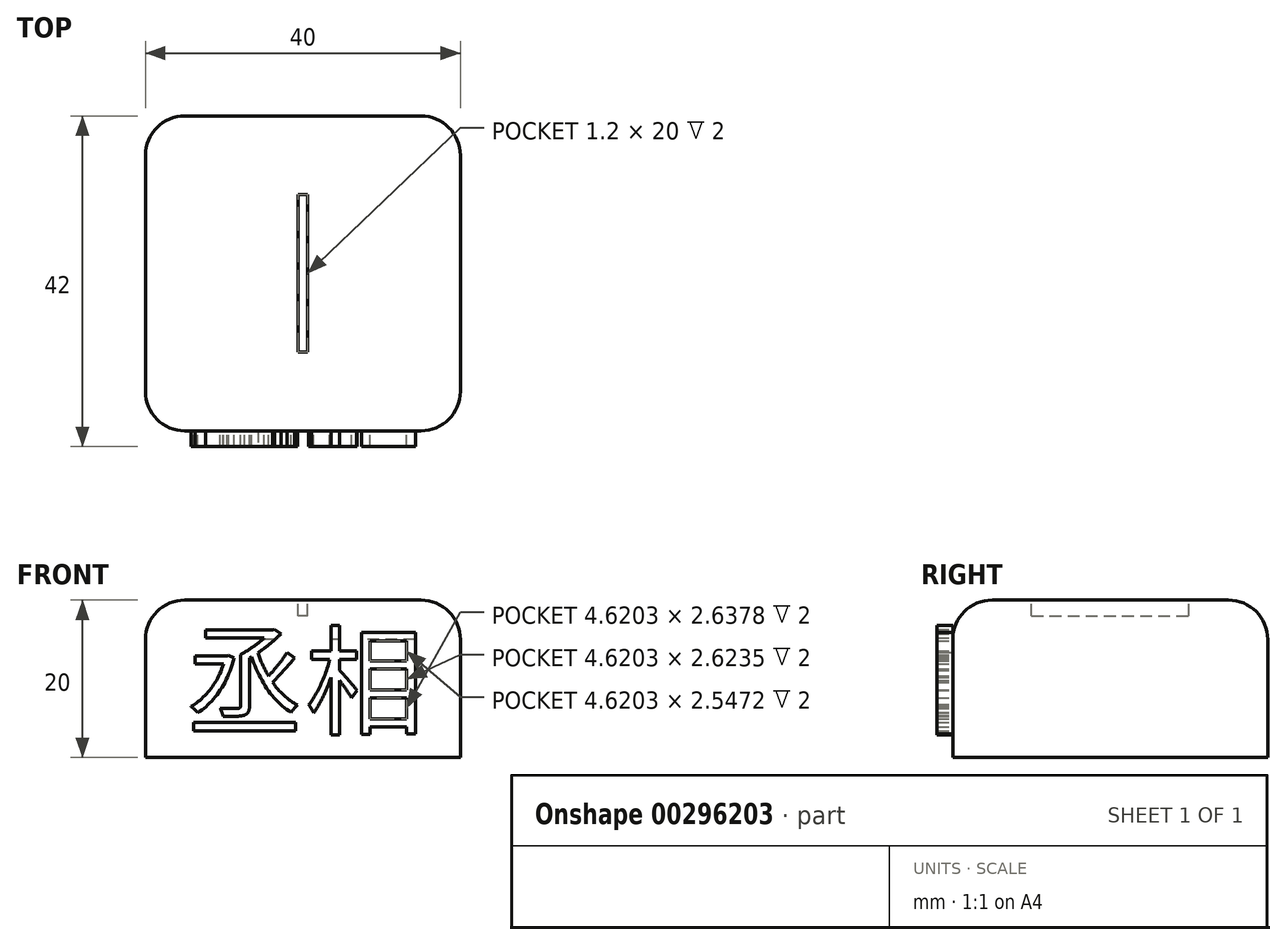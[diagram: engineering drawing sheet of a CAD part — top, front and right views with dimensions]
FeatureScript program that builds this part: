
annotation { "Feature Type Name" : "Feature", "Feature Type Description" : "" }
export const myFeature = defineFeature(function(context is Context, id is Id, definition is map)
    precondition{}
    {
        {
            var Q0;
            Q0=qCreatedBy(makeId("Top.planeOp"),FACE);
            var sketch = newSketch(context, id + "F0", { "sketchPlane" : qUnion([Q0])});
            skLineSegment(sketch, "E0.bottom", {"start": v(20, -20) * mm, "end": v(-20, -20) * mm});
            skLineSegment(sketch, "E0.top", {"start": v(20, 20) * mm, "end": v(-20, 20) * mm});
            skLineSegment(sketch, "E0.left", {"start": v(20, -20) * mm, "end": v(20, 20) * mm});
            skLineSegment(sketch, "E0.right", {"start": v(-20, -20) * mm, "end": v(-20, 20) * mm});
            skPoint(sketch, "E0.middle", {"position": v(0, 0) * mm});
            skLineSegment(sketch, "E1.bottom", {"start": v(0.6, -10) * mm, "end": v(-0.6, -10) * mm});
            skLineSegment(sketch, "E1.top", {"start": v(0.6, 10) * mm, "end": v(-0.6, 10) * mm});
            skLineSegment(sketch, "E1.left", {"start": v(0.6, -10) * mm, "end": v(0.6, 10) * mm});
            skLineSegment(sketch, "E1.right", {"start": v(-0.6, -10) * mm, "end": v(-0.6, 10) * mm});
            skSolve(sketch);
        }
        {
            var Q0;
            Q0=makeQuery(id+"F0.imprint","IMPRINT",FACE,{"disambiguationData":[TD([[makeQuery(id+"F0.imprint","IMPRINT",EDGE,{"derivedFrom":sQuery(id+"F0.wireOp",EDGE,"E0.bottom")}),-1.0]])]});
            var Q1;
            Q1=makeQuery(id+"F0.imprint","IMPRINT",FACE,{"disambiguationData":[TD([[makeQuery(id+"F0.imprint","IMPRINT",EDGE,{"derivedFrom":sQuery(id+"F0.wireOp",EDGE,"E1.bottom")}),-1.0]])]});
            extrude(context, id + "F1", {"entities" : qUnion([Q0, Q1]), "oppositeDirection" : true, "depth" : 20 * mm});
        }
        {
            var Q0;
            Q0=makeQuery(id+"F0.imprint","IMPRINT",FACE,{"disambiguationData":[TD([[makeQuery(id+"F0.imprint","IMPRINT",EDGE,{"derivedFrom":sQuery(id+"F0.wireOp",EDGE,"E1.bottom")}),-1.0]])]});
            extrude(context, id + "F2", {"entities" : qUnion([Q0]), "operationType" : NewBodyOperationType.REMOVE, "oppositeDirection" : true, "depth" : 2 * mm});
        }
        {
            var Q0;
            Q0=makeQuery(id+"F2.boolean.opBoolean","COPY",EDGE,{"derivedFrom":makeQuery(id+"F2.opExtrude","CAP_EDGE",EDGE,{"disambiguationData":[OSD([sQuery(id+"F0.wireOp",EDGE,"E1.left")])],"isStart":true})});
            var Q1;
            Q1=makeQuery(id+"F2.boolean.opBoolean","COPY",EDGE,{"derivedFrom":makeQuery(id+"F2.opExtrude","CAP_EDGE",EDGE,{"disambiguationData":[OSD([sQuery(id+"F0.wireOp",EDGE,"E1.right")])],"isStart":true})});
            var Q2;
            Q2=makeQuery(id+"F1.opExtrude","SWEPT_EDGE",EDGE,{"disambiguationData":[OSD([sQuery(id+"F0.wireOp",EDGE,"E0.bottom"),sQuery(id+"F0.wireOp",EDGE,"E0.left")])]});
            var Q3;
            Q3=makeQuery(id+"F1.opExtrude","SWEPT_EDGE",EDGE,{"disambiguationData":[OSD([sQuery(id+"F0.wireOp",EDGE,"E0.top"),sQuery(id+"F0.wireOp",EDGE,"E0.left")])]});
            var Q4;
            Q4=makeQuery(id+"F1.opExtrude","CAP_EDGE",EDGE,{"disambiguationData":[OSD([sQuery(id+"F0.wireOp",EDGE,"E0.left")])],"isStart":true});
            var Q5;
            Q5=makeQuery(id+"F1.opExtrude","SWEPT_EDGE",EDGE,{"disambiguationData":[OSD([sQuery(id+"F0.wireOp",EDGE,"E0.bottom"),sQuery(id+"F0.wireOp",EDGE,"E0.right")])]});
            var Q6;
            Q6=makeQuery(id+"F1.opExtrude","SWEPT_EDGE",EDGE,{"disambiguationData":[OSD([sQuery(id+"F0.wireOp",EDGE,"E0.top"),sQuery(id+"F0.wireOp",EDGE,"E0.right")])]});
            var Q7;
            Q7=makeQuery(id+"F1.opExtrude","CAP_EDGE",EDGE,{"disambiguationData":[OSD([sQuery(id+"F0.wireOp",EDGE,"E0.top")])],"isStart":true});
            var Q8;
            Q8=makeQuery(id+"F1.opExtrude","CAP_EDGE",EDGE,{"disambiguationData":[OSD([sQuery(id+"F0.wireOp",EDGE,"E0.right")])],"isStart":true});
            var Q9;
            Q9=makeQuery(id+"F1.opExtrude","CAP_EDGE",EDGE,{"disambiguationData":[OSD([sQuery(id+"F0.wireOp",EDGE,"E0.bottom")])],"isStart":true});
            fillet(context, id + "F3", {"entities" : qUnion([Q0, Q1, Q2, Q3, Q4, Q5, Q6, Q7, Q8, Q9]), "radius" : 5 * mm, "tangentPropagation" : true, "allowEdgeOverflow" : false});
        }
        {
            var Q0;
            Q0=makeQuery(id+"F1.opExtrude","SWEPT_FACE",FACE,{"disambiguationData":[OSD([sQuery(id+"F0.wireOp",EDGE,"E0.bottom")])]});
            var sketch = newSketch(context, id + "F4", { "sketchPlane" : qUnion([Q0])});
            skText(sketch, "E2", { "text": "丞相", "fontName": "NotoSansCJKtc-Regular.otf"});
            const initialGuessF4  = {"E2": [-0.015, -0.01598, 1, 0, 0.01098]};
            skSetInitialGuess(sketch, initialGuessF4);
            skSolve(sketch);
        }
        {
            var Q0;
            Q0=makeQuery(id+"F4.imprint","IMPRINT",FACE,{"disambiguationData":[TD([[makeQuery(id+"F4.imprint","IMPRINT",EDGE,{"derivedFrom":sQuery(id+"F4.wireOp",EDGE,"E2.sketch_text.stroke-12")}),1.0]])]});
            var Q1;
            {var subQ0=sQuery(id+"F4.wireOp",EDGE,"E2.sketch_text.stroke-15");Q1=makeQuery(id+"F4.imprint","IMPRINT",FACE,{"disambiguationData":[TD([[makeQuery(id+"F4.imprint","IMPRINT",EDGE,{"derivedFrom":subQ0}),1.0]])]});}
            var Q2;
            Q2=makeQuery(id+"F4.imprint","IMPRINT",FACE,{"disambiguationData":[TD([[makeQuery(id+"F4.imprint","IMPRINT",EDGE,{"derivedFrom":sQuery(id+"F4.wireOp",EDGE,"E2.sketch_text.stroke-0")}),1.0]])]});
            var Q3;
            Q3=makeQuery(id+"F4.imprint","IMPRINT",FACE,{"disambiguationData":[TD([[makeQuery(id+"F4.imprint","IMPRINT",EDGE,{"derivedFrom":sQuery(id+"F4.wireOp",EDGE,"E2.sketch_text.stroke-8")}),1.0]])]});
            var Q4;
            Q4=makeQuery(id+"F4.imprint","IMPRINT",FACE,{"disambiguationData":[TD([[makeQuery(id+"F4.imprint","IMPRINT",EDGE,{"derivedFrom":sQuery(id+"F4.wireOp",EDGE,"E2.sketch_text.stroke-34")}),1.0]])]});
            var Q5;
            {var subQ0=sQuery(id+"F4.wireOp",EDGE,"E2.sketch_text.stroke-38");Q5=makeQuery(id+"F4.imprint","IMPRINT",FACE,{"disambiguationData":[TD([[makeQuery(id+"F4.imprint","IMPRINT",EDGE,{"derivedFrom":subQ0}),1.0]])]});}
            var Q6;
            {var subQ0=sQuery(id+"F4.wireOp",EDGE,"E2.sketch_text.stroke-72");Q6=makeQuery(id+"F4.imprint","IMPRINT",FACE,{"disambiguationData":[TD([[makeQuery(id+"F4.imprint","IMPRINT",EDGE,{"derivedFrom":subQ0}),1.0]])]});}
            var Q7;
            Q7=makeQuery(id+"F4.imprint","IMPRINT",FACE,{"disambiguationData":[TD([[makeQuery(id+"F4.imprint","IMPRINT",EDGE,{"derivedFrom":sQuery(id+"F4.wireOp",EDGE,"E2.sketch_text.stroke-53")}),1.0]])]});
            extrude(context, id + "F5", {"entities" : qUnion([Q0, Q1, Q2, Q3, Q4, Q5, Q6, Q7]), "operationType" : NewBodyOperationType.ADD, "depth" : 2 * mm});
        }
    });
